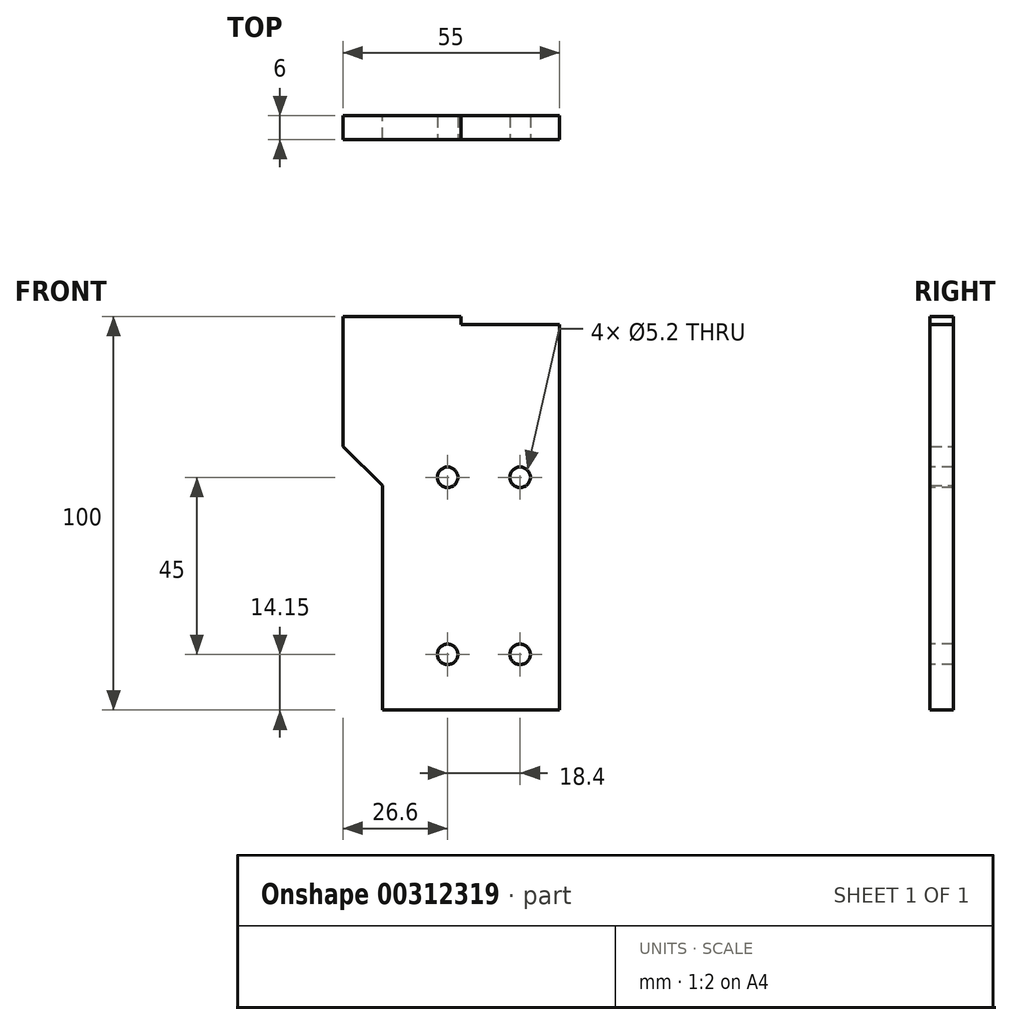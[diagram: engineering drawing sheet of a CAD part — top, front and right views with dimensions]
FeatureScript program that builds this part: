
annotation { "Feature Type Name" : "Feature", "Feature Type Description" : "" }
export const myFeature = defineFeature(function(context is Context, id is Id, definition is map)
    precondition{}
    {
        {
            var Q0;
            Q0=qCreatedBy(makeId("Front.planeOp"),FACE);
            var sketch = newSketch(context, id + "F0", { "sketchPlane" : qUnion([Q0])});
            skLineSegment(sketch, "E0", {"start": v(0, 0) * mm, "end": v(0, 98) * mm});
            skLineSegment(sketch, "E1", {"start": v(0, 98) * mm, "end": v(-25, 98) * mm});
            skLineSegment(sketch, "E2", {"start": v(-25, 98) * mm, "end": v(-25, 100) * mm});
            skLineSegment(sketch, "E3", {"start": v(-25, 100) * mm, "end": v(-55, 100) * mm});
            skLineSegment(sketch, "E4", {"start": v(-55, 100) * mm, "end": v(-55, 67) * mm});
            skLineSegment(sketch, "E5", {"start": v(-55, 67) * mm, "end": v(-45, 57) * mm});
            skLineSegment(sketch, "E6", {"start": v(-45, 57) * mm, "end": v(-45, 0) * mm});
            skLineSegment(sketch, "E7", {"start": v(-45, 0) * mm, "end": v(0, 0) * mm});
            skSolve(sketch);
        }
        {
            var Q0;
            Q0=makeQuery(id+"F0.imprint","IMPRINT",FACE,{"disambiguationData":[TD([[makeQuery(id+"F0.imprint","IMPRINT",EDGE,{"derivedFrom":sQuery(id+"F0.wireOp",EDGE,"E0")}),1.0]])]});
            extrude(context, id + "F1", {"entities" : qUnion([Q0]), "depth" : 6 * mm});
        }
        {
            var Q0;
            Q0=makeQuery(id+"F1.opExtrude","CAP_FACE",FACE,{"disambiguationData":[OSD([sQuery(id+"F0.wireOp",EDGE,"E0"),sQuery(id+"F0.wireOp",EDGE,"E1"),sQuery(id+"F0.wireOp",EDGE,"E2"),sQuery(id+"F0.wireOp",EDGE,"E3"),sQuery(id+"F0.wireOp",EDGE,"E4"),sQuery(id+"F0.wireOp",EDGE,"E5"),sQuery(id+"F0.wireOp",EDGE,"E6"),sQuery(id+"F0.wireOp",EDGE,"E7")])],"isStart":false});
            var sketch = newSketch(context, id + "F2", { "sketchPlane" : qUnion([Q0])});
            skLineSegment(sketch, "E8.bottom", {"start": v(-28.4, 59.15) * mm, "end": v(-10, 59.15) * mm, "construction": true});
            skLineSegment(sketch, "E8.top", {"start": v(-28.4, 14.15) * mm, "end": v(-10, 14.15) * mm, "construction": true});
            skLineSegment(sketch, "E8.left", {"start": v(-28.4, 59.15) * mm, "end": v(-28.4, 14.15) * mm, "construction": true});
            skLineSegment(sketch, "E8.right", {"start": v(-10, 59.15) * mm, "end": v(-10, 14.15) * mm, "construction": true});
            skSolve(sketch);
        }
        {
            var Q0;
            Q0=sQuery(id+"F2.wireOp",VERTEX,"E8.right.start");
            var Q1;
            Q1=sQuery(id+"F2.wireOp",VERTEX,"E8.left.start");
            var Q2;
            Q2=sQuery(id+"F2.wireOp",VERTEX,"E8.left.end");
            var Q3;
            Q3=sQuery(id+"F2.wireOp",VERTEX,"E8.top.end");
            var Q4;
            Q4=makeQuery(id+"F1.opExtrude","SWEPT_BODY",BODY,{"disambiguationData":[OSD([sQuery(id+"F0.wireOp",EDGE,"E0"),sQuery(id+"F0.wireOp",EDGE,"E1"),sQuery(id+"F0.wireOp",EDGE,"E2"),sQuery(id+"F0.wireOp",EDGE,"E3"),sQuery(id+"F0.wireOp",EDGE,"E4"),sQuery(id+"F0.wireOp",EDGE,"E5"),sQuery(id+"F0.wireOp",EDGE,"E6"),sQuery(id+"F0.wireOp",EDGE,"E7")])]});
            hole(context, id + "F3", {"style" : HoleStyle.SIMPLE, "endStyle" : HoleEndStyle.THROUGH, "holeDiameter" : 5.2 * mm, "tappedDepth" : 12 * mm, "tapClearance" : 3, "locations" : qUnion([Q0, Q1, Q2, Q3]), "scope" : qUnion([Q4])});
        }
    });
